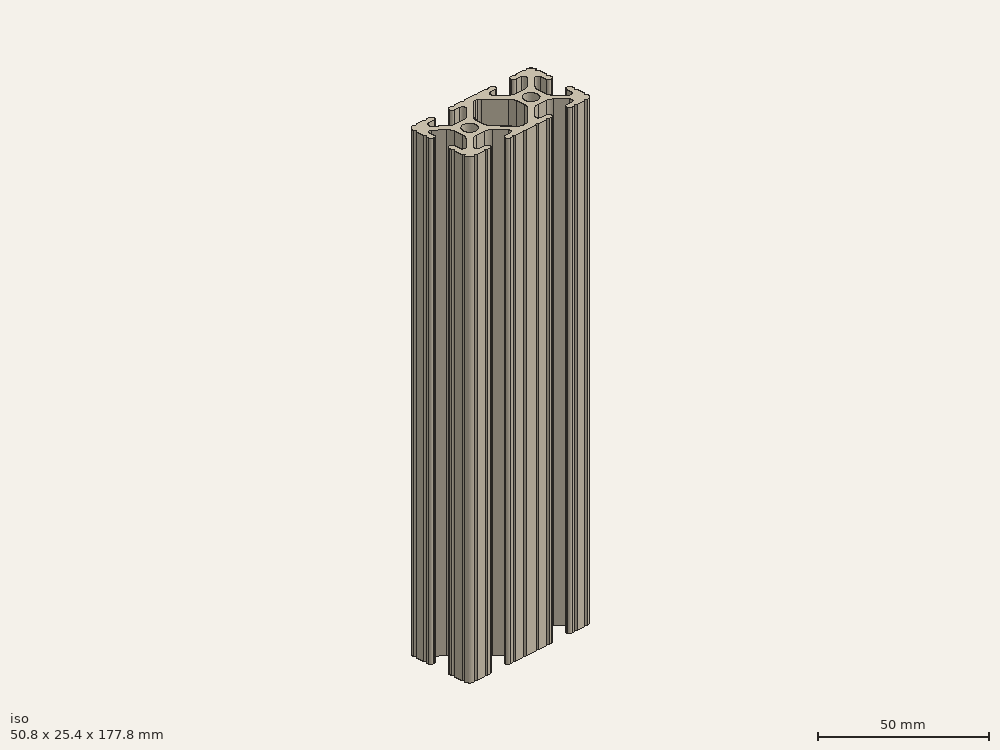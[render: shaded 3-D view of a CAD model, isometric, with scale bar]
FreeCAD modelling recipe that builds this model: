
FCSTD DOCUMENT  (FreeCAD 0.19R23756 (Git))
Label: 1020-7
License: All rights reserved
LicenseURL: http://en.wikipedia.org/wiki/All_rights_reserved
objects: Sketcher::SketchObject×1, Part::Extrusion×1
note: 2 computed .brp shape members not serialized (recipe doc carries the construction recipe); baked Part::Feature solids carry a one-line shape summary decoded from their .brp

FEATURE [Sketcher::SketchObject] Sketch162
  FullyConstrained = false
  sketch-geometry (162):
    g0: LineSegment StartX=7.25951 StartY=3.86941 StartZ=0 EndX=1.54575 EndY=9.57277 EndZ=0
    g1: LineSegment StartX=8.41248 StartY=-10.4902 StartZ=0 EndX=6.28364 EndY=-10.4902 EndZ=0
    g2: ArcOfCircle CenterX=8.41255 CenterY=-11.651 CenterZ=0 NormalX=0 NormalY=0 NormalZ=1 AngleXU=0 Radius=1.04895 StartAngle=4.71239 EndAngle=6.28319
    g3: LineSegment StartX=5.53258 StartY=-8.66607 StartZ=0 EndX=8.80999 EndY=-5.41626 EndZ=0
    g4: LineSegment StartX=9.4615 StartY=-11.651 StartZ=0 EndX=9.4615 EndY=-11.5392 EndZ=0
    g5: ArcOfCircle CenterX=8.41248 CenterY=-11.5392 CenterZ=0 NormalX=0 NormalY=0 NormalZ=1 AngleXU=0 Radius=1.04902 StartAngle=1.15714e-07 EndAngle=1.5708
    g6: ArcOfCircle CenterX=6.28364 CenterY=-9.42351 CenterZ=0 NormalX=0 NormalY=0 NormalZ=1 AngleXU=0 Radius=1.06669 StartAngle=2.35197 EndAngle=4.71239
    g7: LineSegment StartX=-7.28286 StartY=-3.84586 StartZ=0 EndX=-1.67557 EndY=-9.56109 EndZ=0
    g8: LineSegment StartX=1.50403 StartY=-9.57645 StartZ=0 EndX=7.25205 EndY=-3.87684 EndZ=0
    g9: LineSegment StartX=-0.551457 StartY=-10.033 StartZ=0 EndX=0.3952 EndY=-10.033 EndZ=0
    g10: LineSegment StartX=-1.54575 StartY=9.57277 StartZ=0 EndX=-7.25951 EndY=3.86941 EndZ=0
    g11: ArcOfCircle CenterX=0.3952 CenterY=-8.4582 CenterZ=0 NormalX=0 NormalY=0 NormalZ=1 AngleXU=0 Radius=1.5748 StartAngle=4.71239 EndAngle=5.49356
    g12: ArcOfCircle CenterX=5.0165 CenterY=-1.6223 CenterZ=0 NormalX=0 NormalY=0 NormalZ=1 AngleXU=0 Radius=3.175 StartAngle=5.49356 EndAngle=6.28319
    g13: LineSegment StartX=8.1915 StartY=-1.6223 StartZ=0 EndX=8.1915 EndY=1.6223 EndZ=0
    g14: LineSegment StartX=0.433213 StartY=10.033 StartZ=0 EndX=-0.433213 EndY=10.033 EndZ=0
    g15: ArcOfCircle CenterX=-0.551456 CenterY=-8.4582 CenterZ=0 NormalX=0 NormalY=0 NormalZ=1 AngleXU=0 Radius=1.5748 StartAngle=3.91746 EndAngle=4.71239
    g16: ArcOfCircle CenterX=-5.0165 CenterY=1.6223 CenterZ=0 NormalX=0 NormalY=0 NormalZ=1 AngleXU=0 Radius=3.175 StartAngle=2.35528 EndAngle=3.14159
    g17: ArcOfCircle CenterX=-0.433213 CenterY=8.4582 CenterZ=0 NormalX=0 NormalY=0 NormalZ=1 AngleXU=0 Radius=1.5748 StartAngle=1.5708 EndAngle=2.35528
    g18: ArcOfCircle CenterX=5.0165 CenterY=1.6223 CenterZ=0 NormalX=0 NormalY=0 NormalZ=1 AngleXU=0 Radius=3.175 StartAngle=2.15656e-07 EndAngle=0.78631
    g19: Circle CenterX=12.7 CenterY=-2.5e-15 CenterZ=0 NormalX=0 NormalY=0 NormalZ=-1 AngleXU=0 Radius=2.6035
    g20: Circle CenterX=-12.7 CenterY=2.5e-15 CenterZ=0 NormalX=0 NormalY=0 NormalZ=-1 AngleXU=0 Radius=2.6035
    g21: LineSegment StartX=-8.1915 StartY=1.6223 StartZ=0 EndX=-8.1915 EndY=-1.6223 EndZ=0
    g22: LineSegment StartX=-2.13358 StartY=-12.7 StartZ=0 EndX=2.13358 EndY=-12.7 EndZ=0
    g23: ArcOfCircle CenterX=-5.0165 CenterY=-1.6223 CenterZ=0 NormalX=0 NormalY=0 NormalZ=1 AngleXU=0 Radius=3.175 StartAngle=3.14159 EndAngle=3.91746
    g24: LineSegment StartX=3.14958 StartY=-12.7 StartZ=0 EndX=6.3669 EndY=-12.7 EndZ=0
    g25: ArcOfCircle CenterX=6.8749 CenterY=-12.7 CenterZ=0 NormalX=0 NormalY=0 NormalZ=1 AngleXU=0 Radius=0.508 StartAngle=0 EndAngle=3.14159
    g26: LineSegment StartX=-6.28939 StartY=-10.4902 StartZ=0 EndX=-8.41248 EndY=-10.4902 EndZ=0
    g27: LineSegment StartX=-8.41255 StartY=-12.7 StartZ=0 EndX=-7.38288 EndY=-12.7 EndZ=0
    g28: ArcOfCircle CenterX=0.433213 CenterY=8.4582 CenterZ=0 NormalX=0 NormalY=0 NormalZ=1 AngleXU=0 Radius=1.5748 StartAngle=0.78631 EndAngle=1.5708
    g29: ArcOfCircle CenterX=2.64158 CenterY=-12.7 CenterZ=0 NormalX=0 NormalY=0 NormalZ=1 AngleXU=0 Radius=0.508 StartAngle=0 EndAngle=3.14159
    g30: ArcOfCircle CenterX=-16.9875 CenterY=-11.5392 CenterZ=0 NormalX=0 NormalY=0 NormalZ=1 AngleXU=0 Radius=1.04902 StartAngle=1.16223e-07 EndAngle=1.5708
    g31: LineSegment StartX=-8.81696 StartY=-5.44724 StartZ=0 EndX=-5.56415 EndY=-8.76265 EndZ=0
    g32: LineSegment StartX=-16.9875 StartY=-10.4902 StartZ=0 EndX=-19.1164 EndY=-10.4902 EndZ=0
    g33: ArcOfCircle CenterX=-11.0833 CenterY=-7.6708 CenterZ=0 NormalX=0 NormalY=0 NormalZ=1 AngleXU=0 Radius=3.175 StartAngle=0.775866 EndAngle=1.5708
    g34: ArcOfCircle CenterX=-14.3449 CenterY=-7.6708 CenterZ=0 NormalX=0 NormalY=0 NormalZ=1 AngleXU=0 Radius=3.175 StartAngle=1.5708 EndAngle=2.3692
    g35: ArcOfCircle CenterX=-19.1164 CenterY=-9.4742 CenterZ=0 NormalX=0 NormalY=0 NormalZ=1 AngleXU=0 Radius=1.016 StartAngle=2.3692 EndAngle=4.71239
    g36: ArcOfCircle CenterX=-8.41248 CenterY=-11.5392 CenterZ=0 NormalX=0 NormalY=0 NormalZ=1 AngleXU=0 Radius=1.04902 StartAngle=1.5708 EndAngle=3.14159
    g37: LineSegment StartX=7.3829 StartY=-12.7 StartZ=0 EndX=8.41255 EndY=-12.7 EndZ=0
    g38: ArcOfCircle CenterX=-8.41255 CenterY=-11.651 CenterZ=0 NormalX=0 NormalY=0 NormalZ=1 AngleXU=0 Radius=1.04895 StartAngle=3.14159 EndAngle=4.71239
    g39: ArcOfCircle CenterX=14.3545 CenterY=-7.6708 CenterZ=0 NormalX=0 NormalY=0 NormalZ=1 AngleXU=0 Radius=3.175 StartAngle=0.789627 EndAngle=1.5708
    g40: ArcOfCircle CenterX=20.3835 CenterY=-1.55362 CenterZ=0 NormalX=0 NormalY=0 NormalZ=1 AngleXU=0 Radius=3.175 StartAngle=3.14159 EndAngle=3.93122
    g41: LineSegment StartX=23.1902 StartY=6.498 StartZ=0 EndX=23.1902 EndY=4.28752 EndZ=0
    g42: LineSegment StartX=-14.3449 StartY=-4.4958 StartZ=0 EndX=-11.0833 EndY=-4.4958 EndZ=0
    g43: LineSegment StartX=-19.8441 StartY=-8.76517 StartZ=0 EndX=-16.619 EndY=-5.45511 EndZ=0
    g44: LineSegment StartX=-6.36688 StartY=-12.7 StartZ=0 EndX=-3.14958 EndY=-12.7 EndZ=0
    g45: ArcOfCircle CenterX=-6.28939 CenterY=-9.4742 CenterZ=0 NormalX=0 NormalY=0 NormalZ=1 AngleXU=0 Radius=1.016 StartAngle=4.71239 EndAngle=7.05905
    g46: LineSegment StartX=-9.4615 StartY=-11.5392 StartZ=0 EndX=-9.4615 EndY=-11.6511 EndZ=0
    g47: ArcOfCircle CenterX=-6.87488 CenterY=-12.7 CenterZ=0 NormalX=0 NormalY=0 NormalZ=1 AngleXU=0 Radius=0.508 StartAngle=0 EndAngle=3.14159
    g48: LineSegment StartX=-15.9385 StartY=-11.651 StartZ=0 EndX=-15.9385 EndY=-11.5392 EndZ=0
    g49: ArcOfCircle CenterX=-2.64158 CenterY=-12.7 CenterZ=0 NormalX=0 NormalY=0 NormalZ=1 AngleXU=0 Radius=0.508 StartAngle=0 EndAngle=3.14159
    g50: ArcOfCircle CenterX=22.1596 CenterY=-6.33474 CenterZ=0 NormalX=0 NormalY=0 NormalZ=1 AngleXU=0 Radius=1.03057 StartAngle=3.93122 EndAngle=6.28319
    g51: ArcOfCircle CenterX=25.4 CenterY=5.82513 CenterZ=0 NormalX=0 NormalY=0 NormalZ=1 AngleXU=0 Radius=0.508 StartAngle=1.5708 EndAngle=4.71239
    g52: LineSegment StartX=25.4 StartY=6.33313 StartZ=0 EndX=25.4 EndY=9.5504 EndZ=0
    g53: LineSegment StartX=19.0331 StartY=-12.7 StartZ=0 EndX=22.2504 EndY=-12.7 EndZ=0
    g54: ArcOfCircle CenterX=20.3835 CenterY=1.69518 CenterZ=0 NormalX=0 NormalY=0 NormalZ=1 AngleXU=0 Radius=3.175 StartAngle=2.35528 EndAngle=3.14159
    g55: LineSegment StartX=16.9875 StartY=-12.7 StartZ=0 EndX=18.0171 EndY=-12.7 EndZ=0
    g56: ArcOfCircle CenterX=23.2918 CenterY=10.5918 CenterZ=0 NormalX=0 NormalY=0 NormalZ=1 AngleXU=0 Radius=2.1082 StartAngle=6.27114 EndAngle=7.86603
    g57: ArcOfCircle CenterX=24.2392 CenterY=-4.28752 CenterZ=0 NormalX=0 NormalY=0 NormalZ=1 AngleXU=0 Radius=1.04902 StartAngle=1.5708 EndAngle=3.14159
    g58: ArcOfCircle CenterX=24.401 CenterY=-4.23752 CenterZ=0 NormalX=0 NormalY=0 NormalZ=1 AngleXU=0 Radius=0.99902 StartAngle=1.41033e-07 EndAngle=1.5708
    g59: LineSegment StartX=16.59 StartY=-5.41626 StartZ=0 EndX=19.8674 EndY=-8.66607 EndZ=0
    g60: ArcOfCircle CenterX=16.9875 CenterY=-11.5392 CenterZ=0 NormalX=0 NormalY=0 NormalZ=1 AngleXU=0 Radius=1.04902 StartAngle=1.5708 EndAngle=3.14159
    g61: LineSegment StartX=22.2504 StartY=12.7 StartZ=0 EndX=19.0331 EndY=12.7 EndZ=0
    g62: ArcOfCircle CenterX=23.2918 CenterY=-10.5918 CenterZ=0 NormalX=0 NormalY=0 NormalZ=1 AngleXU=0 Radius=2.1082 StartAngle=4.70034 EndAngle=6.29523
    g63: ArcOfCircle CenterX=11.0455 CenterY=-7.6708 CenterZ=0 NormalX=0 NormalY=0 NormalZ=1 AngleXU=0 Radius=3.175 StartAngle=1.5708 EndAngle=2.35197
    g64: ArcOfCircle CenterX=22.7584 CenterY=12.7 CenterZ=0 NormalX=0 NormalY=0 NormalZ=1 AngleXU=0 Radius=0.508 StartAngle=3.14159 EndAngle=6.28288
    g65: LineSegment StartX=19.1164 StartY=-10.4902 StartZ=0 EndX=16.9875 EndY=-10.4902 EndZ=0
    g66: ArcOfCircle CenterX=22.7584 CenterY=-12.7 CenterZ=0 NormalX=0 NormalY=0 NormalZ=1 AngleXU=0 Radius=0.508 StartAngle=0.000301216 EndAngle=3.14159
    g67: ArcOfCircle CenterX=16.9875 CenterY=11.651 CenterZ=0 NormalX=0 NormalY=0 NormalZ=1 AngleXU=0 Radius=1.04902 StartAngle=1.5708 EndAngle=3.14159
    g68: ArcOfCircle CenterX=24.351 CenterY=4.28752 CenterZ=0 NormalX=0 NormalY=0 NormalZ=1 AngleXU=0 Radius=1.04902 StartAngle=4.71239 EndAngle=6.28319
    g69: ArcOfCircle CenterX=19.1164 CenterY=9.4742 CenterZ=0 NormalX=0 NormalY=0 NormalZ=1 AngleXU=0 Radius=1.016 StartAngle=5.49688 EndAngle=7.85398
    g70: LineSegment StartX=19.8341 StartY=8.75512 StartZ=0 EndX=16.4966 EndY=5.42369 EndZ=0
    g71: LineSegment StartX=18.0171 StartY=12.7 StartZ=0 EndX=16.9875 EndY=12.7 EndZ=0
    g72: ArcOfCircle CenterX=18.5251 CenterY=-12.7 CenterZ=0 NormalX=0 NormalY=0 NormalZ=1 AngleXU=0 Radius=0.508 StartAngle=0 EndAngle=3.14159
    g73: LineSegment StartX=15.9384 StartY=11.651 StartZ=0 EndX=15.9384 EndY=11.5392 EndZ=0
    g74: LineSegment StartX=16.9875 StartY=10.4902 StartZ=0 EndX=19.1164 EndY=10.4902 EndZ=0
    g75: LineSegment StartX=11.0455 StartY=-4.4958 StartZ=0 EndX=14.3545 EndY=-4.4958 EndZ=0
    g76: ArcOfCircle CenterX=14.2536 CenterY=7.6708 CenterZ=0 NormalX=0 NormalY=0 NormalZ=1 AngleXU=0 Radius=3.175 StartAngle=4.71239 EndAngle=5.49688
    g77: ArcOfCircle CenterX=25.4 CenterY=-5.82508 CenterZ=0 NormalX=0 NormalY=0 NormalZ=1 AngleXU=0 Radius=0.508 StartAngle=1.5708 EndAngle=4.71239
    g78: LineSegment StartX=18.1405 StartY=3.94229 StartZ=0 EndX=21.4316 EndY=7.22739 EndZ=0
    g79: LineSegment StartX=25.4 StartY=-5.31708 StartZ=0 EndX=25.4 EndY=-4.23752 EndZ=0
    g80: LineSegment StartX=14.2536 StartY=4.4958 StartZ=0 EndX=11.1464 EndY=4.4958 EndZ=0
    g81: ArcOfCircle CenterX=18.5251 CenterY=12.7 CenterZ=0 NormalX=0 NormalY=0 NormalZ=1 AngleXU=0 Radius=0.508 StartAngle=3.14159 EndAngle=6.28319
    g82: LineSegment StartX=23.1902 StartY=-4.28752 StartZ=0 EndX=23.1902 EndY=-6.33474 EndZ=0
    g83: LineSegment StartX=24.401 StartY=-3.2385 StartZ=0 EndX=24.2392 EndY=-3.2385 EndZ=0
    g84: ArcOfCircle CenterX=22.1596 CenterY=6.498 CenterZ=0 NormalX=0 NormalY=0 NormalZ=1 AngleXU=0 Radius=1.03057 StartAngle=0 EndAngle=2.35528
    g85: LineSegment StartX=15.9385 StartY=-11.5392 StartZ=0 EndX=15.9385 EndY=-11.6511 EndZ=0
    g86: LineSegment StartX=25.4 StartY=4.28752 StartZ=0 EndX=25.4 EndY=5.31713 EndZ=0
    g87: ArcOfCircle CenterX=11.1464 CenterY=7.6708 CenterZ=0 NormalX=0 NormalY=0 NormalZ=1 AngleXU=0 Radius=3.175 StartAngle=3.9279 EndAngle=4.71239
    g88: LineSegment StartX=8.90339 StartY=5.42369 StartZ=0 EndX=5.56588 EndY=8.75512 EndZ=0
    g89: LineSegment StartX=21.434 StartY=-7.06654 StartZ=0 EndX=18.148 EndY=-3.80816 EndZ=0
    g90: ArcOfCircle CenterX=25.4 CenterY=10.0584 CenterZ=0 NormalX=0 NormalY=0 NormalZ=1 AngleXU=0 Radius=0.508 StartAngle=1.5711 EndAngle=4.71239
    g91: ArcOfCircle CenterX=16.9875 CenterY=-11.651 CenterZ=0 NormalX=0 NormalY=0 NormalZ=1 AngleXU=0 Radius=1.04895 StartAngle=3.14159 EndAngle=4.71239
    g92: ArcOfCircle CenterX=19.1164 CenterY=-9.42352 CenterZ=0 NormalX=0 NormalY=0 NormalZ=1 AngleXU=0 Radius=1.06668 StartAngle=4.71239 EndAngle=7.07281
    g93: ArcOfCircle CenterX=24.2392 CenterY=4.28752 CenterZ=0 NormalX=0 NormalY=0 NormalZ=1 AngleXU=0 Radius=1.04902 StartAngle=3.14159 EndAngle=4.71239
    g94: ArcOfCircle CenterX=16.9875 CenterY=11.5392 CenterZ=0 NormalX=0 NormalY=0 NormalZ=1 AngleXU=0 Radius=1.04902 StartAngle=3.14159 EndAngle=4.71239
    g95: ArcOfCircle CenterX=25.4 CenterY=-10.0584 CenterZ=0 NormalX=0 NormalY=0 NormalZ=1 AngleXU=0 Radius=0.508 StartAngle=1.5708 EndAngle=4.71209
    g96: ArcOfCircle CenterX=6.87487 CenterY=12.7 CenterZ=0 NormalX=0 NormalY=0 NormalZ=1 AngleXU=0 Radius=0.508 StartAngle=3.14159 EndAngle=6.28319
    g97: LineSegment StartX=25.4 StartY=-9.5504 StartZ=0 EndX=25.4 EndY=-6.33308 EndZ=0
    g98: LineSegment StartX=17.2085 StartY=-1.55362 StartZ=0 EndX=17.2085 EndY=1.69518 EndZ=0
    g99: LineSegment StartX=-9.46155 StartY=11.651 StartZ=0 EndX=-9.46155 EndY=11.5392 EndZ=0
    g100: LineSegment StartX=24.2392 StartY=3.2385 StartZ=0 EndX=24.351 EndY=3.2385 EndZ=0
    g101: LineSegment StartX=-8.41253 StartY=10.4902 StartZ=0 EndX=-6.28939 EndY=10.4902 EndZ=0
    g102: ArcOfCircle CenterX=-10.8409 CenterY=7.6708 CenterZ=0 NormalX=0 NormalY=0 NormalZ=1 AngleXU=0 Radius=3.175 StartAngle=4.71239 EndAngle=5.49688
    g103: LineSegment StartX=-19.1164 StartY=10.4902 StartZ=0 EndX=-16.9875 EndY=10.4902 EndZ=0
    g104: LineSegment StartX=-10.8409 StartY=4.4958 StartZ=0 EndX=-14.1026 EndY=4.4958 EndZ=0
    g105: LineSegment StartX=-16.1879 StartY=5.27664 StartZ=0 EndX=-19.8682 EndY=8.48225 EndZ=0
    g106: LineSegment StartX=-7.38291 StartY=12.7 StartZ=0 EndX=-8.41253 EndY=12.7 EndZ=0
    g107: ArcOfCircle CenterX=-6.28939 CenterY=9.34546 CenterZ=0 NormalX=0 NormalY=0 NormalZ=1 AngleXU=0 Radius=1.14474 StartAngle=5.49688 EndAngle=7.85398
    g108: LineSegment StartX=6.28364 StartY=10.4902 StartZ=0 EndX=8.41253 EndY=10.4902 EndZ=0
    g109: ArcOfCircle CenterX=8.41253 CenterY=11.651 CenterZ=0 NormalX=0 NormalY=0 NormalZ=1 AngleXU=0 Radius=1.04902 StartAngle=4.29175e-07 EndAngle=1.5708
    g110: LineSegment StartX=9.46155 StartY=11.5392 StartZ=0 EndX=9.46155 EndY=11.651 EndZ=0
    g111: ArcOfCircle CenterX=-14.1026 CenterY=7.6708 CenterZ=0 NormalX=0 NormalY=0 NormalZ=1 AngleXU=0 Radius=3.175 StartAngle=3.99583 EndAngle=4.71239
    g112: LineSegment StartX=-5.48068 StartY=8.53527 StartZ=0 EndX=-8.59793 EndY=5.42369 EndZ=0
    g113: ArcOfCircle CenterX=-19.1164 CenterY=9.34546 CenterZ=0 NormalX=0 NormalY=0 NormalZ=1 AngleXU=0 Radius=1.14474 StartAngle=1.5708 EndAngle=3.99583
    g114: LineSegment StartX=8.41253 StartY=12.7 StartZ=0 EndX=7.38287 EndY=12.7 EndZ=0
    g115: LineSegment StartX=-3.14958 StartY=12.7 StartZ=0 EndX=-6.36691 EndY=12.7 EndZ=0
    g116: ArcOfCircle CenterX=-8.41253 CenterY=11.5392 CenterZ=0 NormalX=0 NormalY=0 NormalZ=1 AngleXU=0 Radius=1.04902 StartAngle=3.14159 EndAngle=4.71239
    g117: ArcOfCircle CenterX=8.41253 CenterY=11.5392 CenterZ=0 NormalX=0 NormalY=0 NormalZ=1 AngleXU=0 Radius=1.04902 StartAngle=4.71239 EndAngle=6.28319
    g118: ArcOfCircle CenterX=-6.87491 CenterY=12.7 CenterZ=0 NormalX=0 NormalY=0 NormalZ=1 AngleXU=0 Radius=0.508 StartAngle=3.14159 EndAngle=6.28319
    g119: ArcOfCircle CenterX=-8.41253 CenterY=11.651 CenterZ=0 NormalX=0 NormalY=0 NormalZ=1 AngleXU=0 Radius=1.04902 StartAngle=1.5708 EndAngle=3.14159
    g120: ArcOfCircle CenterX=-2.64159 CenterY=12.7 CenterZ=0 NormalX=0 NormalY=0 NormalZ=1 AngleXU=0 Radius=0.507987 StartAngle=3.14159 EndAngle=6.28319
    g121: ArcOfCircle CenterX=6.28364 CenterY=9.4742 CenterZ=0 NormalX=0 NormalY=0 NormalZ=1 AngleXU=0 Radius=1.016 StartAngle=1.5708 EndAngle=3.9279
    g122: LineSegment StartX=2.13361 StartY=12.7 StartZ=0 EndX=-2.13361 EndY=12.7 EndZ=0
    g123: LineSegment StartX=6.36687 StartY=12.7 StartZ=0 EndX=3.14961 EndY=12.7 EndZ=0
    g124: ArcOfCircle CenterX=-24.401 CenterY=4.23752 CenterZ=0 NormalX=0 NormalY=0 NormalZ=1 AngleXU=0 Radius=0.99902 StartAngle=3.14159 EndAngle=4.71239
    g125: LineSegment StartX=-16.9875 StartY=12.7 StartZ=0 EndX=-18.0171 EndY=12.7 EndZ=0
    g126: LineSegment StartX=-24.401 StartY=3.2385 StartZ=0 EndX=-24.1892 EndY=3.2385 EndZ=0
    g127: ArcOfCircle CenterX=2.64161 CenterY=12.7 CenterZ=0 NormalX=0 NormalY=0 NormalZ=1 AngleXU=0 Radius=0.508 StartAngle=3.14159 EndAngle=6.28319
    g128: ArcOfCircle CenterX=-22.2207 CenterY=-6.67687 CenterZ=0 NormalX=0 NormalY=0 NormalZ=1 AngleXU=0 Radius=0.969476 StartAngle=3.14159 EndAngle=5.51079
    g129: LineSegment StartX=-18.1094 StartY=-3.8465 StartZ=0 EndX=-21.5263 EndY=-7.35342 EndZ=0
    g130: LineSegment StartX=-17.2085 StartY=1.63081 StartZ=0 EndX=-17.2085 EndY=-1.63081 EndZ=0
    g131: ArcOfCircle CenterX=-22.2207 CenterY=6.15588 CenterZ=0 NormalX=0 NormalY=0 NormalZ=1 AngleXU=0 Radius=0.969476 StartAngle=0.854233 EndAngle=3.14159
    g132: LineSegment StartX=-24.1892 StartY=-3.2385 StartZ=0 EndX=-24.401 EndY=-3.2385 EndZ=0
    g133: ArcOfCircle CenterX=-25.4 CenterY=10.0584 CenterZ=0 NormalX=0 NormalY=0 NormalZ=1 AngleXU=0 Radius=0.508 StartAngle=4.71239 EndAngle=7.85368
    g134: LineSegment StartX=-23.1902 StartY=-6.67687 StartZ=0 EndX=-23.1902 EndY=-4.23752 EndZ=0
    g135: ArcOfCircle CenterX=-20.3835 CenterY=-1.63081 CenterZ=0 NormalX=0 NormalY=0 NormalZ=1 AngleXU=0 Radius=3.175 StartAngle=5.51079 EndAngle=6.28319
    g136: ArcOfCircle CenterX=-24.1892 CenterY=-4.23752 CenterZ=0 NormalX=0 NormalY=0 NormalZ=1 AngleXU=0 Radius=0.99902 StartAngle=1.41033e-07 EndAngle=1.5708
    g137: ArcOfCircle CenterX=-25.4 CenterY=5.82508 CenterZ=0 NormalX=0 NormalY=0 NormalZ=1 AngleXU=0 Radius=0.508 StartAngle=4.71239 EndAngle=7.85398
    g138: LineSegment StartX=-23.1902 StartY=4.23752 StartZ=0 EndX=-23.1902 EndY=6.15588 EndZ=0
    g139: LineSegment StartX=-15.9384 StartY=11.5392 StartZ=0 EndX=-15.9384 EndY=11.651 EndZ=0
    g140: ArcOfCircle CenterX=-22.7584 CenterY=12.7 CenterZ=0 NormalX=0 NormalY=0 NormalZ=1 AngleXU=0 Radius=0.508 StartAngle=3.14189 EndAngle=6.28319
    g141: LineSegment StartX=-19.0331 StartY=12.7 StartZ=0 EndX=-22.2504 EndY=12.7 EndZ=0
    g142: ArcOfCircle CenterX=-16.9875 CenterY=11.651 CenterZ=0 NormalX=0 NormalY=0 NormalZ=1 AngleXU=0 Radius=1.04902 StartAngle=4.28571e-07 EndAngle=1.5708
    g143: ArcOfCircle CenterX=-18.5251 CenterY=12.7 CenterZ=0 NormalX=0 NormalY=0 NormalZ=1 AngleXU=0 Radius=0.508 StartAngle=3.14159 EndAngle=6.28319
    g144: ArcOfCircle CenterX=-24.1892 CenterY=4.23752 CenterZ=0 NormalX=0 NormalY=0 NormalZ=1 AngleXU=0 Radius=0.99902 StartAngle=4.71239 EndAngle=6.28319
    g145: LineSegment StartX=-25.4 StartY=5.31708 StartZ=0 EndX=-25.4 EndY=4.23752 EndZ=0
    g146: ArcOfCircle CenterX=-16.9875 CenterY=11.5392 CenterZ=0 NormalX=0 NormalY=0 NormalZ=1 AngleXU=0 Radius=1.04902 StartAngle=4.71239 EndAngle=6.28319
    g147: LineSegment StartX=-21.584 StartY=6.88693 StartZ=0 EndX=-18.2982 EndY=4.02497 EndZ=0
    g148: ArcOfCircle CenterX=-20.3835 CenterY=1.63081 CenterZ=0 NormalX=0 NormalY=0 NormalZ=1 AngleXU=0 Radius=3.175 StartAngle=0 EndAngle=0.854233
    g149: ArcOfCircle CenterX=-23.2918 CenterY=10.5918 CenterZ=0 NormalX=0 NormalY=0 NormalZ=1 AngleXU=0 Radius=2.1082 StartAngle=1.55875 EndAngle=3.15364
    g150: LineSegment StartX=-25.4 StartY=9.5504 StartZ=0 EndX=-25.4 EndY=6.33308 EndZ=0
    g151: LineSegment StartX=-25.4 StartY=-4.23752 StartZ=0 EndX=-25.4 EndY=-5.31708 EndZ=0
    g152: ArcOfCircle CenterX=-23.2918 CenterY=-10.5918 CenterZ=0 NormalX=0 NormalY=0 NormalZ=1 AngleXU=0 Radius=2.1082 StartAngle=3.12954 EndAngle=4.72444
    g153: ArcOfCircle CenterX=-22.7584 CenterY=-12.7 CenterZ=0 NormalX=0 NormalY=0 NormalZ=1 AngleXU=0 Radius=0.508 StartAngle=0 EndAngle=3.14129
    g154: LineSegment StartX=-18.0171 StartY=-12.7 StartZ=0 EndX=-16.9875 EndY=-12.7 EndZ=0
    g155: ArcOfCircle CenterX=-25.4 CenterY=-10.0584 CenterZ=0 NormalX=0 NormalY=0 NormalZ=1 AngleXU=0 Radius=0.508 StartAngle=4.71269 EndAngle=7.85398
    g156: LineSegment StartX=-22.2504 StartY=-12.7 StartZ=0 EndX=-19.0331 EndY=-12.7 EndZ=0
    g157: ArcOfCircle CenterX=-16.9875 CenterY=-11.651 CenterZ=0 NormalX=0 NormalY=0 NormalZ=1 AngleXU=0 Radius=1.04895 StartAngle=4.71239 EndAngle=6.28319
    g158: ArcOfCircle CenterX=-24.401 CenterY=-4.23752 CenterZ=0 NormalX=0 NormalY=0 NormalZ=1 AngleXU=0 Radius=0.99902 StartAngle=1.5708 EndAngle=3.14159
    g159: ArcOfCircle CenterX=-25.4 CenterY=-5.82513 CenterZ=0 NormalX=0 NormalY=0 NormalZ=1 AngleXU=0 Radius=0.508051 StartAngle=4.71239 EndAngle=7.85398
    g160: ArcOfCircle CenterX=-18.5251 CenterY=-12.7 CenterZ=0 NormalX=0 NormalY=0 NormalZ=1 AngleXU=0 Radius=0.508 StartAngle=0 EndAngle=3.14159
    g161: LineSegment StartX=-25.4 StartY=-6.33319 StartZ=0 EndX=-25.4 EndY=-9.5504 EndZ=0
  constraints (160):
    c: Coincident(g161,g155)
    c: Coincident(g159,g161)
    c: Coincident(g151,g159)
    c: Coincident(g158,g151)
    c: Coincident(g124,g145)
    c: Coincident(g137,g145)
    c: Coincident(g137,g150)
    c: Coincident(g133,g150)
    c: Coincident(g152,g155)
    c: Coincident(g149,g133)
    c: Coincident(g158,g132)
    c: Coincident(g124,g126)
    c: Coincident(g136,g132)
    c: Coincident(g144,g126)
    c: Coincident(g153,g152)
    c: Coincident(g140,g149)
    c: Coincident(g134,g128)
    c: Coincident(g134,g136)
    c: Coincident(g138,g144)
    c: Coincident(g131,g138)
    c: Coincident(g153,g156)
    c: Coincident(g141,g140)
    c: Coincident(g131,g147)
    c: Coincident(g129,g128)
    c: Coincident(g105,g113)
    c: Coincident(g35,g43)
    c: Coincident(g35,g32)
    c: Coincident(g113,g103)
    c: Coincident(g156,g160)
    c: Coincident(g143,g141)
    c: Coincident(g147,g148)
    c: Coincident(g135,g129)
    c: Coincident(g154,g160)
    c: Coincident(g143,g125)
    c: Coincident(g130,g135)
    c: Coincident(g130,g148)
    c: Coincident(g154,g157)
    c: Coincident(g32,g30)
    c: Coincident(g103,g146)
    c: Coincident(g142,g125)
    c: Coincident(g43,g34)
    c: Coincident(g111,g105)
    c: Coincident(g157,g48)
    c: Coincident(g48,g30)
    c: Coincident(g139,g146)
    c: Coincident(g139,g142)
    c: Coincident(g42,g34)
    c: Coincident(g104,g111)
    c: Coincident(g33,g42)
    c: Coincident(g102,g104)
    c: Coincident(g38,g46)
    c: Coincident(g46,g36)
    c: Coincident(g99,g116)
    c: Coincident(g119,g99)
    c: Coincident(g33,g31)
    c: Coincident(g102,g112)
    c: Coincident(g27,g38)
    c: Coincident(g36,g26)
    c: Coincident(g116,g101)
    c: Coincident(g106,g119)
    c: Coincident(g21,g23)
    c: Coincident(g21,g16)
    c: Coincident(g27,g47)
    c: Coincident(g106,g118)
    c: Coincident(g23,g7)
    c: Coincident(g10,g16)
    c: Coincident(g44,g47)
    c: Coincident(g118,g115)
    c: Coincident(g45,g26)
    c: Coincident(g107,g101)
    c: Coincident(g45,g31)
    c: Coincident(g112,g107)
    c: Coincident(g44,g49)
    c: Coincident(g120,g115)
    c: Coincident(g22,g49)
    c: Coincident(g122,g120)
    c: Coincident(g15,g7)
    c: Coincident(g10,g17)
    c: Coincident(g9,g15)
    c: Coincident(g17,g14)
    c: Coincident(g9,g11)
    c: Coincident(g14,g28)
    c: Coincident(g8,g11)
    c: Coincident(g0,g28)
    c: Coincident(g29,g22)
    c: Coincident(g122,g127)
    c: Coincident(g24,g29)
    c: Coincident(g123,g127)
    c: Coincident(g3,g6)
    c: Coincident(g88,g121)
    c: Coincident(g1,g6)
    c: Coincident(g108,g121)
    c: Coincident(g25,g24)
    c: Coincident(g96,g123)
    c: Coincident(g8,g12)
    c: Coincident(g18,g0)
    c: Coincident(g25,g37)
    c: Coincident(g96,g114)
    c: Coincident(g12,g13)
    c: Coincident(g18,g13)
    c: Coincident(g2,g37)
    c: Coincident(g5,g1)
    c: Coincident(g117,g108)
    c: Coincident(g109,g114)
    c: Coincident(g3,g63)
    c: Coincident(g87,g88)
    c: Coincident(g2,g4)
    c: Coincident(g5,g4)
    c: Coincident(g117,g110)
    c: Coincident(g109,g110)
    c: Coincident(g75,g63)
    c: Coincident(g80,g87)
    c: Coincident(g80,g76)
    c: Coincident(g39,g75)
    c: Coincident(g85,g91)
    c: Coincident(g85,g60)
    c: Coincident(g73,g94)
    c: Coincident(g73,g67)
    c: Coincident(g70,g76)
    c: Coincident(g59,g39)
    c: Coincident(g55,g91)
    c: Coincident(g60,g65)
    c: Coincident(g94,g74)
    c: Coincident(g67,g71)
    c: Coincident(g40,g98)
    c: Coincident(g54,g98)
    c: Coincident(g55,g72)
    c: Coincident(g71,g81)
    c: Coincident(g78,g54)
    c: Coincident(g40,g89)
    c: Coincident(g53,g72)
    c: Coincident(g61,g81)
    c: Coincident(g65,g92)
    c: Coincident(g74,g69)
    c: Coincident(g70,g69)
    c: Coincident(g59,g92)
    c: Coincident(g84,g78)
    c: Coincident(g50,g89)
    c: Coincident(g53,g66)
    c: Coincident(g64,g61)
    c: Coincident(g82,g50)
    c: Coincident(g57,g82)
    c: Coincident(g41,g93)
    c: Coincident(g41,g84)
    c: Coincident(g62,g66)
    c: Coincident(g64,g56)
    c: Coincident(g57,g83)
    c: Coincident(g100,g93)
    c: Coincident(g100,g68)
    c: Coincident(g58,g83)
    c: Coincident(g62,g95)
    c: Coincident(g56,g90)
    c: Coincident(g97,g95)
    c: Coincident(g97,g77)
    c: Coincident(g77,g79)
    c: Coincident(g58,g79)
    c: Coincident(g68,g86)
    c: Coincident(g86,g51)
    c: Coincident(g51,g52)
    c: Coincident(g52,g90)
FEATURE [Part::Extrusion] Extrude
  Base = -> Sketch162
  Dir = (0,0,1)
  DirMode = 2
  FaceMakerClass = Part::FaceMakerBullseye
  LengthFwd = 177.8
  LengthRev = 0
  Solid = true
  Symmetric = false
